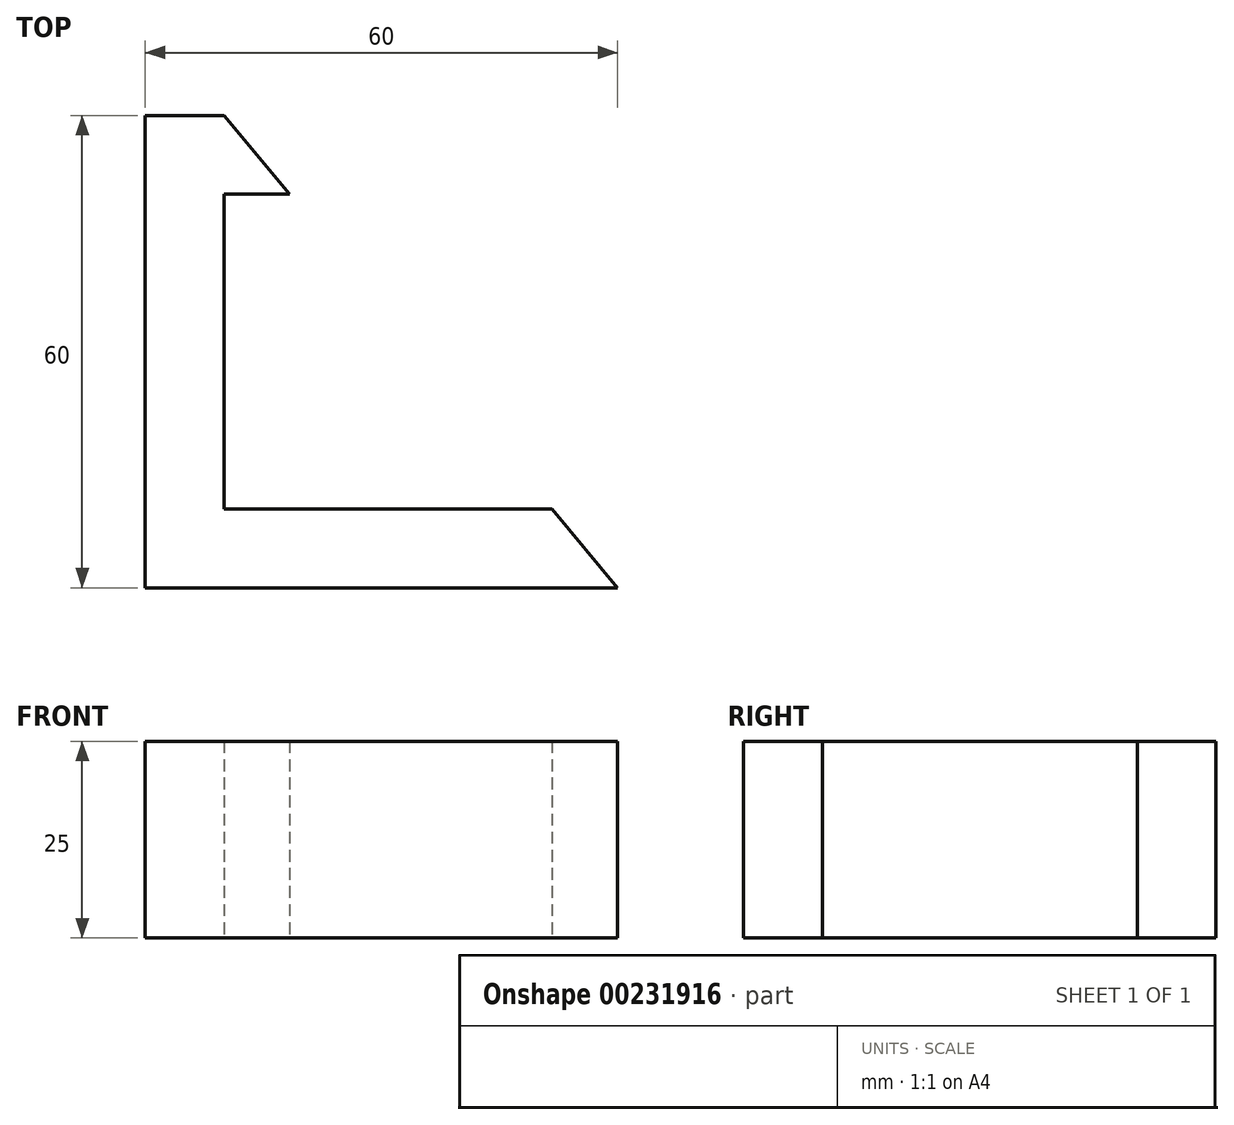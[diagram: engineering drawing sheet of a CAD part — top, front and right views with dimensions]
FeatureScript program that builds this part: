
annotation { "Feature Type Name" : "Feature", "Feature Type Description" : "" }
export const myFeature = defineFeature(function(context is Context, id is Id, definition is map)
    precondition{}
    {
        {
            var Q0;
            Q0=qCreatedBy(makeId("Top.planeOp"),FACE);
            var sketch = newSketch(context, id + "F0", { "sketchPlane" : qUnion([Q0])});
            skLineSegment(sketch, "E0.bottom", {"start": v(0, 0) * mm, "end": v(60, 0) * mm});
            skLineSegment(sketch, "E0.left", {"start": v(0, 0) * mm, "end": v(0, 60) * mm});
            skLineSegment(sketch, "E1.left", {"start": v(10, 10) * mm, "end": v(10, 50) * mm});
            skLineSegment(sketch, "E2", {"start": v(0, 60) * mm, "end": v(10, 60) * mm});
            skLineSegment(sketch, "E3", {"start": v(10, 50) * mm, "end": v(18.33, 50) * mm});
            skLineSegment(sketch, "E4", {"start": v(10, 10) * mm, "end": v(51.67, 10) * mm});
            skLineSegment(sketch, "E5", {"start": v(10, 60) * mm, "end": v(18.33, 50) * mm});
            skLineSegment(sketch, "E6", {"start": v(51.67, 10) * mm, "end": v(60, 0) * mm});
            skSolve(sketch);
        }
        {
            var Q0;
            Q0=makeQuery(id+"F0.imprint","IMPRINT",FACE,{"disambiguationData":[TD([[makeQuery(id+"F0.imprint","IMPRINT",EDGE,{"derivedFrom":sQuery(id+"F0.wireOp",EDGE,"E0.bottom")}),1.0]])]});
            extrude(context, id + "F1", {"entities" : qUnion([Q0]), "depth" : 25 * mm});
        }
    });
